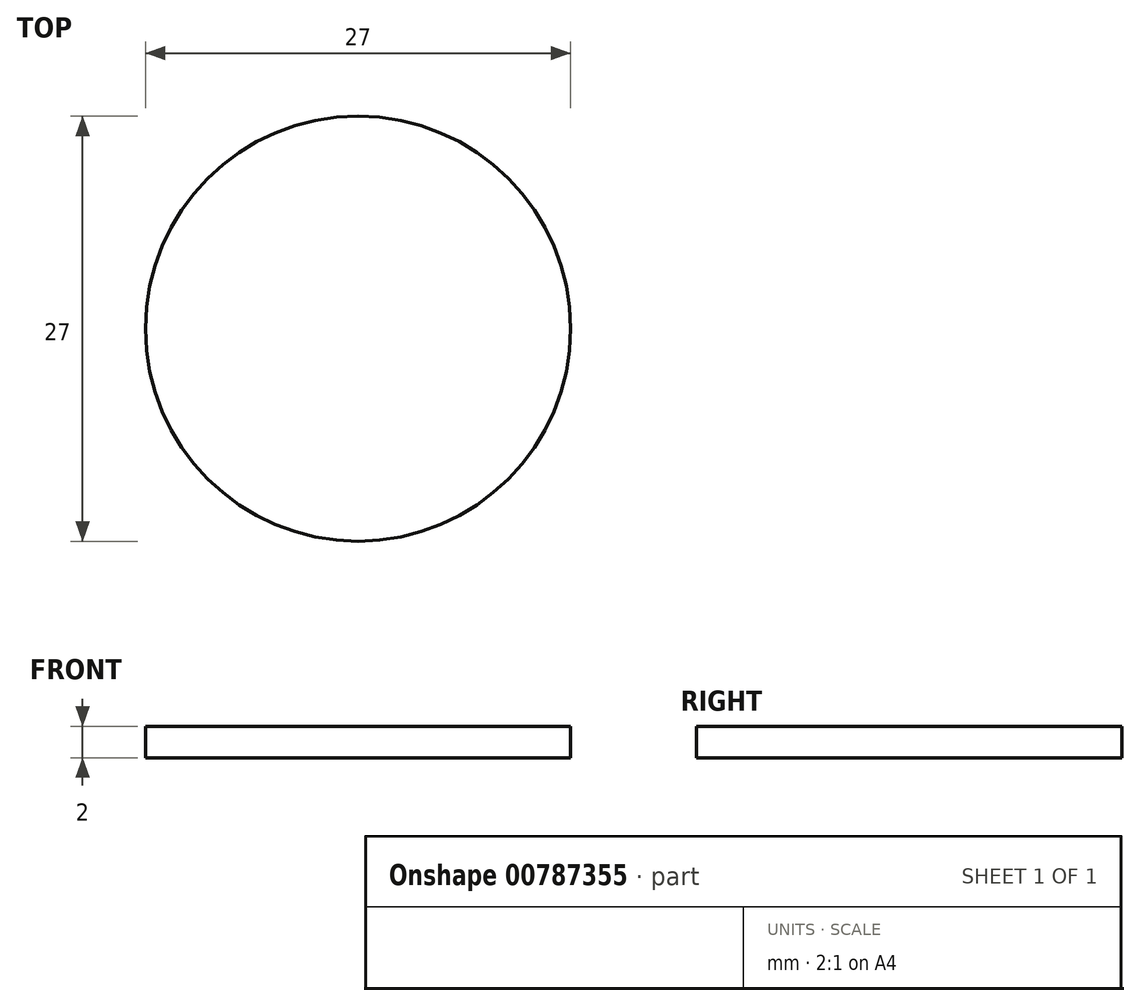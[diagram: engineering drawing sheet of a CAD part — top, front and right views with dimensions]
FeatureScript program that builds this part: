
annotation { "Feature Type Name" : "Feature", "Feature Type Description" : "" }
export const myFeature = defineFeature(function(context is Context, id is Id, definition is map)
    precondition{}
    {
        {
            var Q0;
            Q0=qCreatedBy(makeId("Top.planeOp"),FACE);
            var sketch = newSketch(context, id + "F0", { "sketchPlane" : qUnion([Q0])});
            skCircle(sketch, "E0", {"center": v(0, 0) * mm, "radius": 13.5 * mm});
            skSolve(sketch);
        }
        {
            var Q0;
            Q0 = qSketchRegion(id + "F0", true);
            extrude(context, id + "F1", {"entities" : qUnion([Q0]), "depth" : 2 * mm, "offsetDistance" : 25 * mm});
        }
    });
